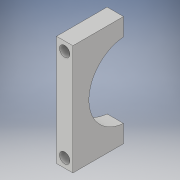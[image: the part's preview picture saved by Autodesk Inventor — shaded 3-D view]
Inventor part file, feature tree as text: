
AUTODESK INVENTOR PART (.ipt)
format: ipt  version: 2019 (Build 230136000, 136)  size: 138,752 bytes
history: native  units: mm
features: sketch x3, extrude x2, hole x1
ambient origin geometry x8: Origin, YZ Plane, XZ Plane, XY Plane, X Axis, Y Axis, Z Axis, Center Point
bodies: Solid1 (feature_tree)
feature tree (6):
  sketch  "Sketch1"  dims[d0=5.5mm d1=37.0mm]
  extrude  "Extrusion1"  Depth=37.0mm
  hole  "Hole1"  [1 undecoded]
  extrude  "Extrusion2"  Depth=17.0mm TaperAngle=0.0deg
  sketch  "Sketch2"  dims[d2=3.0mm d3=2.75mm]
  sketch  "Sketch3"  dims[d4=3.0mm d5=5.5mm d6=37.0mm d7=3.0mm d8=2.75mm d9=3.0mm d10=5.5mm d11=37.0mm d12=3.0mm d13=2.75mm d14=3.0mm d15=5.5mm d16=37.0mm d17=3.0mm d18=2.75mm d19=3.0mm d20=5.5mm d21=37.0mm d22=3.0mm d23=2.75mm d24=3.0mm d25=5.5mm d26=37.0mm d27=3.0mm d28=2.75mm d29=3.0mm d30=5.5mm d31=37.0mm d32=3.0mm d33=2.75mm d34=3.0mm d35=5.5mm d36=37.0mm d37=3.0mm d38=2.75mm d39=3.0mm d40=17.0mm d41=0.0mm d42=3.5mm d43=6.0mm d44=4.0mm d45=2.0mm d46=90.0deg d47=8.0mm d48=20.594885mm d49=18.0mm d50=25.25mm d51=5.5mm d52=0.0mm]
note: 1 required parameter value undecoded (feature->parameter linkage not recoverable at this tier; creation-order binding heuristic only, values carry confidence <= 0.55)
